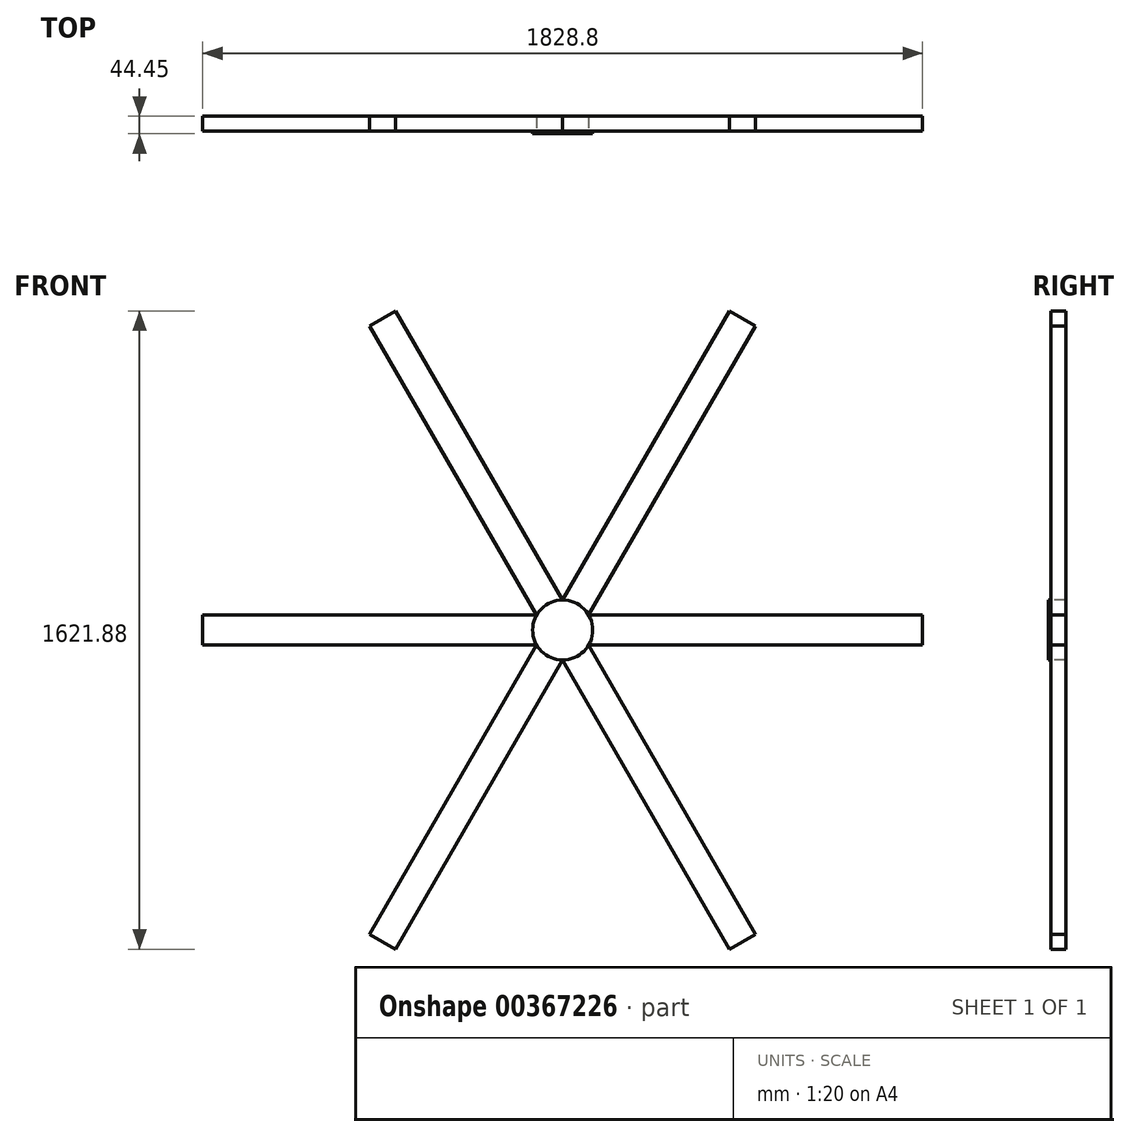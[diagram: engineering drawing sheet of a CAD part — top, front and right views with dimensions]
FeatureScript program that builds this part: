
annotation { "Feature Type Name" : "Feature", "Feature Type Description" : "" }
export const myFeature = defineFeature(function(context is Context, id is Id, definition is map)
    precondition{}
    {
        {
            var Q0;
            Q0=qCreatedBy(makeId("Front.planeOp"),FACE);
            var sketch = newSketch(context, id + "F0", { "sketchPlane" : qUnion([Q0])});
            skLineSegment(sketch, "E0", {"start": v(0, 0) * mm, "end": v(914.4, 0) * mm});
            skLineSegment(sketch, "E1", {"start": v(0, 0) * mm, "end": v(457.2, 791.9) * mm});
            skLineSegment(sketch, "E2", {"start": v(0, 0) * mm, "end": v(-457.2, 791.9) * mm});
            skLineSegment(sketch, "E3", {"start": v(0, 0) * mm, "end": v(-914.4, 0) * mm});
            skLineSegment(sketch, "E4", {"start": v(0, 0) * mm, "end": v(-457.2, -791.9) * mm});
            skLineSegment(sketch, "E5", {"start": v(0, 0) * mm, "end": v(457.2, -791.9) * mm});
            skLineSegment(sketch, "E6", {"start": v(914.4, 0) * mm, "end": v(914.4, -38.1) * mm});
            skLineSegment(sketch, "E7", {"start": v(914.4, -38.1) * mm, "end": v(-914.4, -38.1) * mm});
            skLineSegment(sketch, "E8", {"start": v(-914.4, -38.1) * mm, "end": v(-914.4, 0) * mm});
            skLineSegment(sketch, "E9", {"start": v(-914.4, 38.1) * mm, "end": v(914.4, 38.1) * mm});
            skLineSegment(sketch, "E10", {"start": v(-914.4, 0) * mm, "end": v(-914.4, 38.1) * mm});
            skLineSegment(sketch, "E11", {"start": v(914.4, 0) * mm, "end": v(914.4, 38.1) * mm});
            skLineSegment(sketch, "E12", {"start": v(457.2, -791.9) * mm, "end": v(490.2, -772.84) * mm});
            skLineSegment(sketch, "E13", {"start": v(490.2, -772.84) * mm, "end": v(66, -38.1) * mm});
            skLineSegment(sketch, "E14", {"start": v(457.2, -791.9) * mm, "end": v(424.2, -810.94) * mm});
            skLineSegment(sketch, "E15", {"start": v(424.2, -810.94) * mm, "end": v(-22, -38.1) * mm});
            skLineSegment(sketch, "E16", {"start": v(-457.2, 791.9) * mm, "end": v(-490.2, 772.84) * mm});
            skLineSegment(sketch, "E17", {"start": v(-490.2, 772.84) * mm, "end": v(-66, 38.1) * mm});
            skLineSegment(sketch, "E18", {"start": v(-457.2, 791.9) * mm, "end": v(-424.2, 810.94) * mm});
            skLineSegment(sketch, "E19", {"start": v(-424.2, 810.94) * mm, "end": v(22, 38.1) * mm});
            skLineSegment(sketch, "E20", {"start": v(457.2, 791.9) * mm, "end": v(424.2, 810.94) * mm});
            skLineSegment(sketch, "E21", {"start": v(424.2, 810.94) * mm, "end": v(0, 76.2) * mm});
            skLineSegment(sketch, "E22", {"start": v(457.2, 791.9) * mm, "end": v(490.2, 772.84) * mm});
            skLineSegment(sketch, "E23", {"start": v(490.2, 772.84) * mm, "end": v(66, 38.1) * mm});
            skLineSegment(sketch, "E24", {"start": v(-457.2, -791.9) * mm, "end": v(-490.2, -772.84) * mm});
            skLineSegment(sketch, "E25", {"start": v(-490.2, -772.84) * mm, "end": v(-66, -38.1) * mm});
            skLineSegment(sketch, "E26", {"start": v(-457.2, -791.9) * mm, "end": v(-424.2, -810.94) * mm});
            skLineSegment(sketch, "E27", {"start": v(-424.2, -810.94) * mm, "end": v(0, -76.2) * mm});
            skSolve(sketch);
        }
        {
            var Q0;
            {var subQ1=sQuery(id+"F0.wireOp",EDGE,"E14");Q0=makeQuery(id+"F0.imprint","IMPRINT",FACE,{"disambiguationData":[TD([[makeQuery(id+"F0.imprint","IMPRINT",EDGE,{"derivedFrom":subQ1}),-1.0]])]});}
            var Q1;
            {var subQ0=sQuery(id+"F0.wireOp",EDGE,"E12");Q1=makeQuery(id+"F0.imprint","IMPRINT",FACE,{"disambiguationData":[TD([[makeQuery(id+"F0.imprint","IMPRINT",EDGE,{"derivedFrom":subQ0}),1.0]])]});}
            var Q2;
            {var subQ3=sQuery(id+"F0.wireOp",EDGE,"E0");Q2=makeQuery(id+"F0.imprint","IMPRINT",FACE,{"disambiguationData":[TD([[makeQuery(id+"F0.imprint","IMPRINT",EDGE,{"derivedFrom":subQ3}),-1.0]])]});}
            var Q3;
            {var subQ4=sQuery(id+"F0.wireOp",EDGE,"E0");Q3=makeQuery(id+"F0.imprint","IMPRINT",FACE,{"disambiguationData":[TD([[makeQuery(id+"F0.imprint","IMPRINT",EDGE,{"derivedFrom":subQ4}),1.0]])]});}
            var Q4;
            {var subQ0=sQuery(id+"F0.wireOp",EDGE,"E22");Q4=makeQuery(id+"F0.imprint","IMPRINT",FACE,{"disambiguationData":[TD([[makeQuery(id+"F0.imprint","IMPRINT",EDGE,{"derivedFrom":subQ0}),-1.0]])]});}
            var Q5;
            {var subQ0=sQuery(id+"F0.wireOp",EDGE,"E20");Q5=makeQuery(id+"F0.imprint","IMPRINT",FACE,{"disambiguationData":[TD([[makeQuery(id+"F0.imprint","IMPRINT",EDGE,{"derivedFrom":subQ0}),1.0]])]});}
            var Q6;
            {var subQ1=sQuery(id+"F0.wireOp",EDGE,"E18");Q6=makeQuery(id+"F0.imprint","IMPRINT",FACE,{"disambiguationData":[TD([[makeQuery(id+"F0.imprint","IMPRINT",EDGE,{"derivedFrom":subQ1}),-1.0]])]});}
            var Q7;
            {var subQ0=sQuery(id+"F0.wireOp",EDGE,"E16");Q7=makeQuery(id+"F0.imprint","IMPRINT",FACE,{"disambiguationData":[TD([[makeQuery(id+"F0.imprint","IMPRINT",EDGE,{"derivedFrom":subQ0}),1.0]])]});}
            var Q8;
            {var subQ4=sQuery(id+"F0.wireOp",EDGE,"E3");Q8=makeQuery(id+"F0.imprint","IMPRINT",FACE,{"disambiguationData":[TD([[makeQuery(id+"F0.imprint","IMPRINT",EDGE,{"derivedFrom":subQ4}),1.0]])]});}
            var Q9;
            {var subQ3=sQuery(id+"F0.wireOp",EDGE,"E3");Q9=makeQuery(id+"F0.imprint","IMPRINT",FACE,{"disambiguationData":[TD([[makeQuery(id+"F0.imprint","IMPRINT",EDGE,{"derivedFrom":subQ3}),-1.0]])]});}
            var Q10;
            {var subQ0=sQuery(id+"F0.wireOp",EDGE,"E24");Q10=makeQuery(id+"F0.imprint","IMPRINT",FACE,{"disambiguationData":[TD([[makeQuery(id+"F0.imprint","IMPRINT",EDGE,{"derivedFrom":subQ0}),-1.0]])]});}
            var Q11;
            {var subQ0=sQuery(id+"F0.wireOp",EDGE,"E26");Q11=makeQuery(id+"F0.imprint","IMPRINT",FACE,{"disambiguationData":[TD([[makeQuery(id+"F0.imprint","IMPRINT",EDGE,{"derivedFrom":subQ0}),1.0]])]});}
            var Q12;
            {var subQ0=sQuery(id+"F0.wireOp",EDGE,"E2");var subQ3=sQuery(id+"F0.wireOp",EDGE,"E9");var subQ5=makeQuery(id+"F0.imprint","INTERSECT",VERTEX,{"derivedFrom":[subQ0,subQ3]});Q12=makeQuery(id+"F0.imprint","IMPRINT",FACE,{"disambiguationData":[TD([[makeQuery(id+"F0.imprint","IMPRINT",EDGE,{"disambiguationData":[TD([[subQ5,-1.0]])],"derivedFrom":subQ3}),-1.0]])]});}
            var Q13;
            {var subQ0=sQuery(id+"F0.wireOp",EDGE,"E5");var subQ3=sQuery(id+"F0.wireOp",EDGE,"E7");var subQ5=makeQuery(id+"F0.imprint","INTERSECT",VERTEX,{"derivedFrom":[subQ0,subQ3]});Q13=makeQuery(id+"F0.imprint","IMPRINT",FACE,{"disambiguationData":[TD([[makeQuery(id+"F0.imprint","IMPRINT",EDGE,{"disambiguationData":[TD([[subQ5,-1.0]])],"derivedFrom":subQ3}),-1.0]])]});}
            extrude(context, id + "F1", {"entities" : qUnion([Q0, Q1, Q2, Q3, Q4, Q5, Q6, Q7, Q8, Q9, Q10, Q11, Q12, Q13]), "oppositeDirection" : true, "depth" : 38.1 * mm});
        }
        {
            var Q0;
            Q0=makeQuery(id+"F1.opExtrude","CAP_FACE",FACE,{"disambiguationData":[OSD([sQuery(id+"F0.wireOp",EDGE,"E6"),sQuery(id+"F0.wireOp",EDGE,"E7"),sQuery(id+"F0.wireOp",EDGE,"E8"),sQuery(id+"F0.wireOp",EDGE,"E9"),sQuery(id+"F0.wireOp",EDGE,"E10"),sQuery(id+"F0.wireOp",EDGE,"E11"),sQuery(id+"F0.wireOp",EDGE,"E12"),sQuery(id+"F0.wireOp",EDGE,"E13"),sQuery(id+"F0.wireOp",EDGE,"E14"),sQuery(id+"F0.wireOp",EDGE,"E15"),sQuery(id+"F0.wireOp",EDGE,"E16"),sQuery(id+"F0.wireOp",EDGE,"E17"),sQuery(id+"F0.wireOp",EDGE,"E18"),sQuery(id+"F0.wireOp",EDGE,"E19"),sQuery(id+"F0.wireOp",EDGE,"E20"),sQuery(id+"F0.wireOp",EDGE,"E21"),sQuery(id+"F0.wireOp",EDGE,"E22"),sQuery(id+"F0.wireOp",EDGE,"E23"),sQuery(id+"F0.wireOp",EDGE,"E24"),sQuery(id+"F0.wireOp",EDGE,"E25"),sQuery(id+"F0.wireOp",EDGE,"E26"),sQuery(id+"F0.wireOp",EDGE,"E27")])],"isStart":true});
            var sketch = newSketch(context, id + "F2", { "sketchPlane" : qUnion([Q0])});
            skCircle(sketch, "E28", {"center": v(0, 0) * mm, "radius": 76.2 * mm});
            skSolve(sketch);
        }
        {
            var Q0;
            {var subQ0=sQuery(id+"F2.wireOp",EDGE,"E28");var subQ8=makeQuery(id+"F2.imprint","INTERSECT",VERTEX,{"derivedFrom":[makeQuery(id+"F1.opExtrude","CAP_EDGE",EDGE,{"disambiguationData":[OSD([sQuery(id+"F0.wireOp",EDGE,"E19")])],"isStart":true}),makeQuery(id+"F1.opExtrude","CAP_EDGE",EDGE,{"disambiguationData":[OSD([sQuery(id+"F0.wireOp",EDGE,"E21")])],"isStart":true}),subQ0]});Q0=makeQuery(id+"F2.imprint","IMPRINT",FACE,{"disambiguationData":[TD([[makeQuery(id+"F2.imprint","IMPRINT",EDGE,{"disambiguationData":[TD([[subQ8,1.0]])],"derivedFrom":subQ0}),1.0]])]});}
            extrude(context, id + "F3", {"entities" : qUnion([Q0]), "operationType" : NewBodyOperationType.ADD, "depth" : 6.35 * mm});
        }
    });
